# Revit family: Haworth_ImprovSide_Chair_SledBase
name_source: partatom
category: Furniture
revit_build: Autodesk Revit 2018 (Build: 20170223_1515(x64)
units: mm (PartAtom-declared; Revit-internal decimal feet)

## family parameters
Always vertical = Yes
Cut with Voids When Loaded = No
OmniClass Number = 23.40.20.00
OmniClass Title = General Furniture and Specialties
Room Calculation Point = No
Shared = No
Work Plane-Based = No

## types (2) — shared parameters
Actual Depth = 1' - 10 11/16"
Actual Height = 2' - 8"
Actual Width = 1' - 8 13/16"
Arm Cap Finish = Haworth _ Polymer _ Fog
Assembly Code = E2020200
Depth = 21.5 in.
Description = Haworth - Chair - Improv - Side - Sled
Frame Finish = Haworth _ Paint _ Graphite
Height = 32 in.
Manufacturer = Haworth
Model = Haworth - Chair - Improv - Side - Sled
Revision = 2
Seat Finish = Haworth _ Fabric _ Tellure _ Tomato 3A-43
Size = Verify Final Dim. w/ Haworth
Sustainability Info = http://www.haworth.com
URL = http://haworth.com
URL - Product = http://www.haworth.com
Warranty = http://www.haworth.com
Width = 22 in.

## per-type parameters (varying)
| type | Front Leg Height | Front Void Offset | With Arms |
| Without Arms | 1' - 5 17/32" | -0' - 2" | No |
| With Arms | 1' - 11 1/2" | -0' - 0 1/4" | Yes |

type visibility flags (boolean, named after types; folded from table):
- Without Arms: Yes: Without Arms
- With Arms: Yes: (none)

## geometry (parser evidence)
native form markers: Sweep x2
no freeform markers — native parametric forms only
